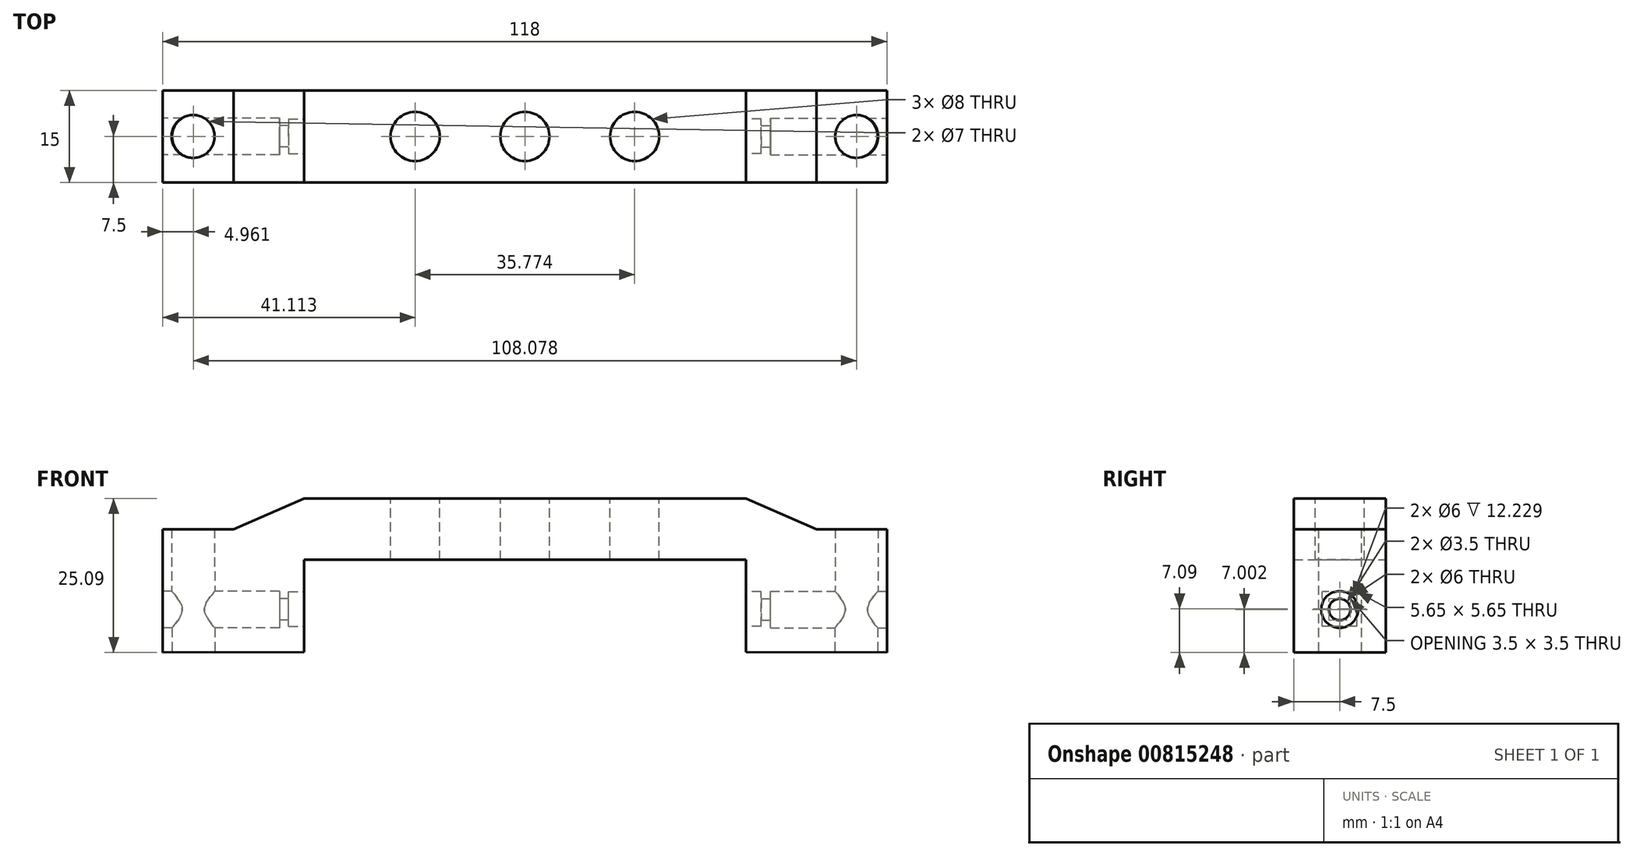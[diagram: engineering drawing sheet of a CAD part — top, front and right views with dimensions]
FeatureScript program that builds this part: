
annotation { "Feature Type Name" : "Feature", "Feature Type Description" : "" }
export const myFeature = defineFeature(function(context is Context, id is Id, definition is map)
    precondition{}
    {
        {
            var Q0;
            Q0=qCreatedBy(makeId("Front.planeOp"),FACE);
            var sketch = newSketch(context, id + "F0", { "sketchPlane" : qUnion([Q0])});
            skLineSegment(sketch, "E0.bottom", {"start": v(-36, 5) * mm, "end": v(36, 5) * mm});
            skLineSegment(sketch, "E0.top", {"start": v(-36, -5) * mm, "end": v(36, -5) * mm});
            skLineSegment(sketch, "E0.left", {"start": v(-36, 5) * mm, "end": v(-36, -5) * mm});
            skLineSegment(sketch, "E0.right", {"start": v(36, 5) * mm, "end": v(36, -5) * mm});
            skPoint(sketch, "E0.middle", {"position": v(0, 0) * mm});
            skLineSegment(sketch, "E1", {"start": v(36, 0) * mm, "end": v(21, 0) * mm});
            skLineSegment(sketch, "E2", {"start": v(-36, -5) * mm, "end": v(-59, -5) * mm});
            skLineSegment(sketch, "E3", {"start": v(-59, -20.09) * mm, "end": v(-36, -20) * mm});
            skLineSegment(sketch, "E4", {"start": v(-36, -20) * mm, "end": v(-36, -5) * mm});
            skLineSegment(sketch, "E5", {"start": v(-59, -5) * mm, "end": v(-59, -20.09) * mm});
            skLineSegment(sketch, "E6.MirrorCS", {"start": v(59, -5) * mm, "end": v(59, -20.09) * mm});
            skLineSegment(sketch, "E7.MirrorCS", {"start": v(36, -20) * mm, "end": v(36, -5) * mm});
            skLineSegment(sketch, "E8.MirrorCS", {"start": v(59, -20.09) * mm, "end": v(36, -20) * mm});
            skLineSegment(sketch, "E9", {"start": v(36, 0) * mm, "end": v(59, 0) * mm});
            skLineSegment(sketch, "E10", {"start": v(59, 0) * mm, "end": v(59, -5) * mm});
            skLineSegment(sketch, "E11.MirrorCS", {"start": v(-36, 0) * mm, "end": v(-59, 0) * mm});
            skLineSegment(sketch, "E12.MirrorCS", {"start": v(-59, 0) * mm, "end": v(-59, -5) * mm});
            skLineSegment(sketch, "E13.left", {"start": v(36, 5) * mm, "end": v(36, 2.5) * mm});
            skLineSegment(sketch, "E13.right", {"start": v(66, 7.5) * mm, "end": v(66, 5) * mm});
            skLineSegment(sketch, "E14", {"start": v(36, 5) * mm, "end": v(47.5, 0) * mm});
            skLineSegment(sketch, "E15.MirrorCS", {"start": v(-36, 5) * mm, "end": v(-47.5, 0) * mm});
            skSolve(sketch);
        }
        {
            var Q0;
            {var subQ6=sQuery(id+"F0.wireOp",EDGE,"E14");var subQ10=sQuery(id+"F0.wireOp",EDGE,"E15.MirrorCS");var subQ12=sQuery(id+"F0.wireOp",EDGE,"E0.bottom");var subQ17=sQuery(id+"F0.wireOp",EDGE,"E2");var subQ24=makeQuery(id+"F0.imprint","IMPRINT",EDGE,{"derivedFrom":subQ17});Q0=qUnion([makeQuery(id+"F0.imprint","IMPRINT",FACE,{"disambiguationData":[TD([[makeQuery(id+"F0.imprint","IMPRINT",EDGE,{"derivedFrom":subQ6}),-1.0]])]}),makeQuery(id+"F0.imprint","IMPRINT",FACE,{"disambiguationData":[TD([[subQ24,1.0]])]}),makeQuery(id+"F0.imprint","IMPRINT",FACE,{"disambiguationData":[TD([[subQ24,-1.0]])]}),makeQuery(id+"F0.imprint","IMPRINT",FACE,{"disambiguationData":[TD([[makeQuery(id+"F0.imprint","IMPRINT",EDGE,{"derivedFrom":subQ10}),1.0]])]}),makeQuery(id+"F0.imprint","IMPRINT",FACE,{"disambiguationData":[TD([[makeQuery(id+"F0.imprint","IMPRINT",EDGE,{"derivedFrom":subQ12}),-1.0]])]}),makeQuery(id+"F0.imprint","IMPRINT",FACE,{"disambiguationData":[TD([[makeQuery(id+"F0.imprint","IMPRINT",EDGE,{"derivedFrom":sQuery(id+"F0.wireOp",EDGE,"E6.MirrorCS")}),-1.0]])]})]);}
            extrude(context, id + "F1", {"entities" : qUnion([Q0]), "depth" : 15 * mm, "offsetDistance" : 25 * mm});
        }
        {
            var Q0;
            Q0=makeQuery(id+"F1.opExtrude","SWEPT_FACE",FACE,{"disambiguationData":[OSD([sQuery(id+"F0.wireOp",EDGE,"E8.MirrorCS")])]});
            var sketch = newSketch(context, id + "F2", { "sketchPlane" : qUnion([Q0])});
            skLineSegment(sketch, "E16", {"start": v(59.08, 7.5) * mm, "end": v(54.08, 7.5) * mm});
            skCircle(sketch, "E17", {"center": v(54.08, 7.5) * mm, "radius": 3.5 * mm});
            skSolve(sketch);
        }
        {
            var Q0;
            Q0=makeQuery(id+"F1.opExtrude","SWEPT_FACE",FACE,{"disambiguationData":[OSD([sQuery(id+"F0.wireOp",EDGE,"E6.MirrorCS"),sQuery(id+"F0.wireOp",EDGE,"E10")])]});
            var sketch = newSketch(context, id + "F3", { "sketchPlane" : qUnion([Q0])});
            skLineSegment(sketch, "E18", {"start": v(-7.5, -20.09) * mm, "end": v(-7.5, -13.09) * mm});
            skCircle(sketch, "E19", {"center": v(-7.5, -13.09) * mm, "radius": 3 * mm});
            skCircle(sketch, "E20", {"center": v(-7.5, -13.09) * mm, "radius": 1.75 * mm});
            skSolve(sketch);
        }
        {
            var Q0;
            Q0=makeQuery(id+"F1.opExtrude","SWEPT_FACE",FACE,{"disambiguationData":[OSD([sQuery(id+"F0.wireOp",EDGE,"E7.MirrorCS")])]});
            var sketch = newSketch(context, id + "F4", { "sketchPlane" : qUnion([Q0])});
            skLineSegment(sketch, "E21", {"start": v(7.5, -20) * mm, "end": v(7.5, -13) * mm});
            skLineSegment(sketch, "E22.bottom", {"start": v(10.32, -15.82) * mm, "end": v(4.68, -15.82) * mm});
            skLineSegment(sketch, "E22.top", {"start": v(10.32, -10.17) * mm, "end": v(4.67, -10.17) * mm});
            skLineSegment(sketch, "E22.left", {"start": v(10.32, -15.82) * mm, "end": v(10.32, -10.17) * mm});
            skLineSegment(sketch, "E22.right", {"start": v(4.68, -15.82) * mm, "end": v(4.67, -10.17) * mm});
            skPoint(sketch, "E22.middle", {"position": v(7.5, -13) * mm});
            skSolve(sketch);
        }
        {
            var Q0;
            Q0=makeQuery(id+"F3.imprint","IMPRINT",FACE,{"disambiguationData":[TD([[makeQuery(id+"F3.imprint","IMPRINT",EDGE,{"derivedFrom":sQuery(id+"F3.wireOp",EDGE,"E20")}),1.0]])]});
            extrude(context, id + "F5", {"entities" : qUnion([Q0]), "operationType" : NewBodyOperationType.REMOVE, "oppositeDirection" : true, "depth" : 23 * mm, "offsetDistance" : 25 * mm});
        }
        {
            var Q0;
            Q0=makeQuery(id+"F3.imprint","IMPRINT",FACE,{"disambiguationData":[TD([[makeQuery(id+"F3.imprint","IMPRINT",EDGE,{"derivedFrom":sQuery(id+"F3.wireOp",EDGE,"E19")}),1.0]])]});
            extrude(context, id + "F6", {"entities" : qUnion([Q0]), "operationType" : NewBodyOperationType.REMOVE, "oppositeDirection" : true, "depth" : 19 * mm, "offsetDistance" : 25 * mm});
        }
        {
            var Q0;
            Q0=makeQuery(id+"F2.imprint","IMPRINT",FACE,{"disambiguationData":[TD([[makeQuery(id+"F2.imprint","IMPRINT",EDGE,{"derivedFrom":sQuery(id+"F2.wireOp",EDGE,"E17")}),1.0]])]});
            extrude(context, id + "F7", {"entities" : qUnion([Q0]), "operationType" : NewBodyOperationType.REMOVE, "oppositeDirection" : true, "depth" : 25 * mm, "offsetDistance" : 25 * mm});
        }
        {
            var Q0;
            Q0=makeQuery(id+"F4.imprint","IMPRINT",FACE,{"disambiguationData":[TD([[makeQuery(id+"F4.imprint","IMPRINT",EDGE,{"derivedFrom":sQuery(id+"F4.wireOp",EDGE,"E22.top")}),1.0]])]});
            extrude(context, id + "F8", {"entities" : qUnion([Q0]), "operationType" : NewBodyOperationType.REMOVE, "oppositeDirection" : true, "depth" : 2.5 * mm, "offsetDistance" : 25 * mm});
        }
        {
            var Q0;
            Q0=makeQuery(id+"F1.opExtrude","SWEPT_FACE",FACE,{"disambiguationData":[OSD([sQuery(id+"F0.wireOp",EDGE,"E5"),sQuery(id+"F0.wireOp",EDGE,"E12.MirrorCS")])]});
            var sketch = newSketch(context, id + "F9", { "sketchPlane" : qUnion([Q0])});
            skLineSegment(sketch, "E23", {"start": v(7.5, -20.09) * mm, "end": v(7.5, -13.09) * mm});
            skCircle(sketch, "E24", {"center": v(7.5, -13.09) * mm, "radius": 1.75 * mm});
            skCircle(sketch, "E25", {"center": v(7.5, -13.09) * mm, "radius": 3 * mm});
            skSolve(sketch);
        }
        {
            var Q0;
            Q0=makeQuery(id+"F1.opExtrude","SWEPT_FACE",FACE,{"disambiguationData":[OSD([sQuery(id+"F0.wireOp",EDGE,"E4")])]});
            var sketch = newSketch(context, id + "F10", { "sketchPlane" : qUnion([Q0])});
            skLineSegment(sketch, "E26", {"start": v(-7.5, -20) * mm, "end": v(-7.5, -13) * mm});
            skLineSegment(sketch, "E27.bottom", {"start": v(-4.68, -15.82) * mm, "end": v(-10.33, -15.82) * mm});
            skLineSegment(sketch, "E27.top", {"start": v(-4.68, -10.17) * mm, "end": v(-10.32, -10.17) * mm});
            skLineSegment(sketch, "E27.left", {"start": v(-4.68, -15.82) * mm, "end": v(-4.68, -10.17) * mm});
            skLineSegment(sketch, "E27.right", {"start": v(-10.33, -15.82) * mm, "end": v(-10.32, -10.17) * mm});
            skPoint(sketch, "E27.middle", {"position": v(-7.5, -13) * mm});
            skSolve(sketch);
        }
        {
            var Q0;
            Q0=makeQuery(id+"F1.opExtrude","SWEPT_FACE",FACE,{"disambiguationData":[OSD([sQuery(id+"F0.wireOp",EDGE,"E3")])]});
            var sketch = newSketch(context, id + "F11", { "sketchPlane" : qUnion([Q0])});
            skLineSegment(sketch, "E28", {"start": v(-59.08, 7.5) * mm, "end": v(-54.08, 7.5) * mm});
            skCircle(sketch, "E29", {"center": v(-54.08, 7.5) * mm, "radius": 3.5 * mm});
            skSolve(sketch);
        }
        {
            var Q0;
            Q0=makeQuery(id+"F9.imprint","IMPRINT",FACE,{"disambiguationData":[TD([[makeQuery(id+"F9.imprint","IMPRINT",EDGE,{"derivedFrom":sQuery(id+"F9.wireOp",EDGE,"E24")}),-1.0]])]});
            extrude(context, id + "F12", {"entities" : qUnion([Q0]), "operationType" : NewBodyOperationType.REMOVE, "oppositeDirection" : true, "depth" : 19 * mm, "offsetDistance" : 25 * mm});
        }
        {
            var Q0;
            Q0=makeQuery(id+"F9.imprint","IMPRINT",FACE,{"disambiguationData":[TD([[makeQuery(id+"F9.imprint","IMPRINT",EDGE,{"derivedFrom":sQuery(id+"F9.wireOp",EDGE,"E24")}),1.0]])]});
            extrude(context, id + "F13", {"entities" : qUnion([Q0]), "operationType" : NewBodyOperationType.REMOVE, "oppositeDirection" : true, "depth" : 23 * mm, "offsetDistance" : 25 * mm});
        }
        {
            var Q0;
            Q0=makeQuery(id+"F10.imprint","IMPRINT",FACE,{"disambiguationData":[TD([[makeQuery(id+"F10.imprint","IMPRINT",EDGE,{"derivedFrom":sQuery(id+"F10.wireOp",EDGE,"E27.top")}),1.0]])]});
            extrude(context, id + "F14", {"entities" : qUnion([Q0]), "operationType" : NewBodyOperationType.REMOVE, "oppositeDirection" : true, "depth" : 2.5 * mm, "offsetDistance" : 25 * mm});
        }
        {
            var Q0;
            Q0=makeQuery(id+"F11.imprint","IMPRINT",FACE,{"disambiguationData":[TD([[makeQuery(id+"F11.imprint","IMPRINT",EDGE,{"derivedFrom":sQuery(id+"F11.wireOp",EDGE,"E29")}),1.0]])]});
            extrude(context, id + "F15", {"entities" : qUnion([Q0]), "operationType" : NewBodyOperationType.REMOVE, "oppositeDirection" : true, "depth" : 25 * mm, "offsetDistance" : 25 * mm});
        }
        {
            var Q0;
            Q0=makeQuery(id+"F1.opExtrude","SWEPT_FACE",FACE,{"disambiguationData":[OSD([sQuery(id+"F0.wireOp",EDGE,"E0.bottom")])]});
            var sketch = newSketch(context, id + "F16", { "sketchPlane" : qUnion([Q0])});
            skLineSegment(sketch, "E30", {"start": v(-36, -7.5) * mm, "end": v(36, -7.5) * mm});
            skCircle(sketch, "E31", {"center": v(0, -7.5) * mm, "radius": 4 * mm});
            skCircle(sketch, "E32", {"center": v(-17.89, -7.5) * mm, "radius": 4 * mm});
            skCircle(sketch, "E33.MirrorC", {"center": v(17.89, -7.5) * mm, "radius": 4 * mm});
            skSolve(sketch);
        }
        {
            var Q0;
            Q0 = qSketchRegion(id + "F16", true);
            extrude(context, id + "F17", {"entities" : qUnion([Q0]), "operationType" : NewBodyOperationType.REMOVE, "oppositeDirection" : true, "depth" : 25 * mm, "offsetDistance" : 25 * mm});
        }
    });
